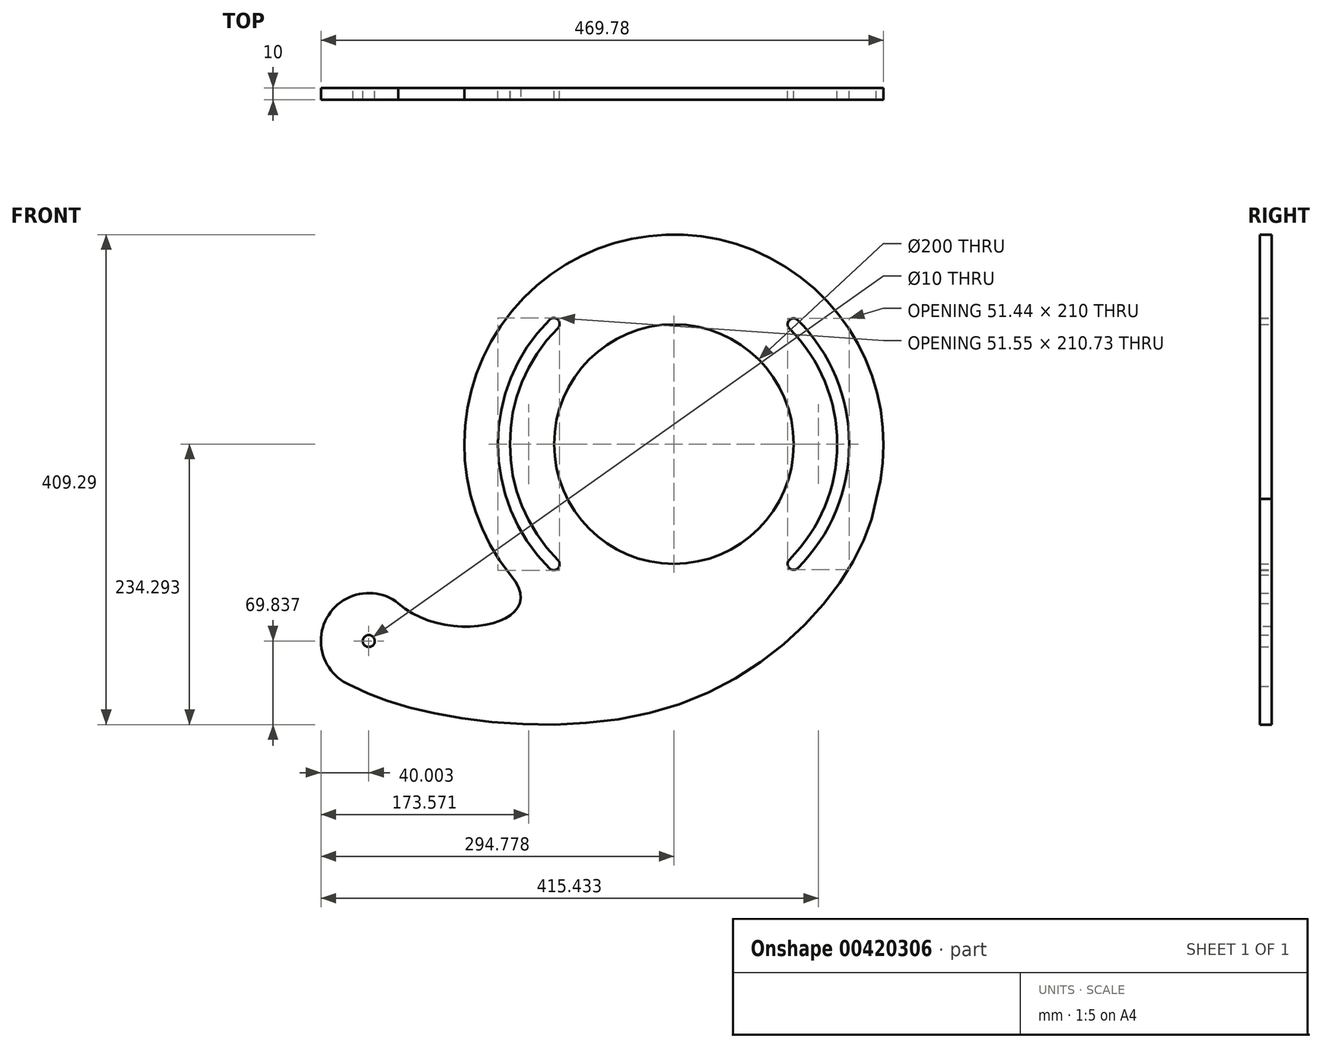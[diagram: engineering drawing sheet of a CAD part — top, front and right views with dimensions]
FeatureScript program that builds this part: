
annotation { "Feature Type Name" : "Feature", "Feature Type Description" : "" }
export const myFeature = defineFeature(function(context is Context, id is Id, definition is map)
    precondition{}
    {
        {
            var Q0;
            Q0=qCreatedBy(makeId("Front.planeOp"),FACE);
            var sketch = newSketch(context, id + "F0", { "sketchPlane" : qUnion([Q0])});
            skArc(sketch, "E0", {"start": v(169.15, -45.62) * mm, "mid": v(-35.4, 171.51) * mm, "end": v(-136.36, -109.2) * mm});
            skFitSpline(sketch, "E1", {"points": [v(169.15, -45.62) * mm, v(0, -218.71) * mm, v(-267.66, -202.06) * mm], "startDerivative": vector(-57.79, -380.6) * mm, "endDerivative": vector(-250.37, 144.35) * mm});
            skArc(sketch, "E2", {"start": v(-229.81, -132.82) * mm, "mid": v(-289.63, -145.09) * mm, "end": v(-267.66, -202.06) * mm});
            skFitSpline(sketch, "E3", {"points": [v(-229.81, -132.82) * mm, v(-136.36, -109.2) * mm], "startDerivative": vector(123.49, -110) * mm, "endDerivative": vector(-110.66, 123.78) * mm});
            skCircle(sketch, "E4", {"center": v(0.25, 0.18) * mm, "radius": 100 * mm});
            skCircle(sketch, "E5", {"center": v(-254.53, -164.27) * mm, "radius": 5 * mm});
            skCircle(sketch, "E6.cCircle", {"center": v(0, 0) * mm, "radius": 100.18 * mm, "construction": true});
            skPoint(sketch, "E6.0.midPoint", {"position": v(0, 100.18) * mm});
            skArc(sketch, "E7.0", {"start": v(-96.65, -96.65) * mm, "mid": v(-136.74, 0.18) * mm, "end": v(-96.65, 97.01) * mm});
            skArc(sketch, "E8.0", {"start": v(-103.72, -103.72) * mm, "mid": v(-146.74, 0.18) * mm, "end": v(-103.72, 104.08) * mm});
            skArc(sketch, "E9.0", {"start": v(96.65, 96.65) * mm, "mid": v(136.62, 0.18) * mm, "end": v(96.65, -96.28) * mm});
            skArc(sketch, "E10.0", {"start": v(103.72, 103.72) * mm, "mid": v(146.62, 0.18) * mm, "end": v(103.72, -103.35) * mm});
            skArc(sketch, "E11", {"start": v(-96.65, 97.01) * mm, "mid": v(-96.65, 104.08) * mm, "end": v(-103.72, 104.08) * mm});
            skArc(sketch, "E12", {"start": v(-103.72, -103.72) * mm, "mid": v(-96.65, -103.72) * mm, "end": v(-96.65, -96.65) * mm});
            skArc(sketch, "E13", {"start": v(103.72, 103.72) * mm, "mid": v(96.65, 103.72) * mm, "end": v(96.65, 96.65) * mm});
            skArc(sketch, "E14", {"start": v(96.65, -96.28) * mm, "mid": v(96.65, -103.35) * mm, "end": v(103.72, -103.35) * mm});
            skSolve(sketch);
        }
        {
            var Q0;
            Q0=makeQuery(id+"F0.imprint","IMPRINT",FACE,{"disambiguationData":[TD([[makeQuery(id+"F0.imprint","IMPRINT",EDGE,{"derivedFrom":sQuery(id+"F0.wireOp",EDGE,"E0")}),1.0]])]});
            extrude(context, id + "F1", {"entities" : qUnion([Q0]), "depth" : 10 * mm});
        }
    });
